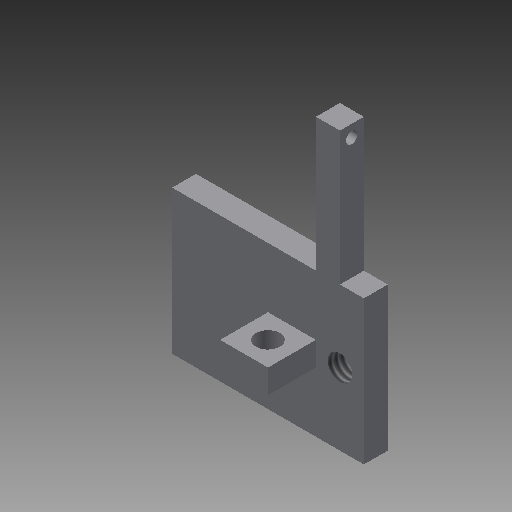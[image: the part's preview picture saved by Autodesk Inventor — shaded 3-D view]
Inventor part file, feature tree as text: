
AUTODESK INVENTOR PART (.ipt)
format: ipt  version: 2017 (Build 210142000, 142)  size: 135,680 bytes
history: native  units: in
note: dims shown in document units (in); Inventor stores cm internally (conversion verified against a paired STEP export)
features: sketch x6, hole x3, projected_geometry x3, extrude x2
ambient origin geometry x8: Origin, YZ Plane, XZ Plane, XY Plane, X Axis, Y Axis, Z Axis, Center Point
bodies: Solid1 (feature_tree)
feature tree (14):
  extrude  "Extrusion1"  Depth=1.0in
  extrude  "Extrusion2"  Depth=0.695in
  hole  "Hole1"  [1 undecoded]
  hole  "Hole2"  [1 undecoded]
  hole  "Hole3"  [1 undecoded]
  sketch  "Sketch6"  dims[d15=0.06in d16=0.75in d17=0.375in d18=0.25in d19=0.5635in d20=1.0in d21=0.8108in d22=0.125in d23=0.125in d24=0.75in d25=0.375in d26=0.25in d27=0.5635in d28=1.0in d29=0.8108in d30=0.13in d31=0.75in d32=0.375in d33=0.25in d34=0.5635in d35=1.0in d36=0.8108in d37=0.125in d38=0.063in]
  sketch  "Sketch1"  dims[d0=0.75in d2=1.0in]
  sketch  "Sketch2"  dims[d3=0.125in d4=0.695in]
  sketch  "Sketch3"  dims[d5=0.125in d6=0.0in d7=0.125in]
  projected_geometry  "Projected Loop1"
  sketch  "Sketch4"  dims[d10=0.25in d11=0.3125in]
  projected_geometry  "Projected Loop2"
  sketch  "Sketch5"  dims[d12=0.25in d13=0.25in d14=0.0in]
  projected_geometry  "Projected Loop3"
note: 3 required parameter values undecoded (feature->parameter linkage not recoverable at this tier; creation-order binding heuristic only, values carry confidence <= 0.55)
